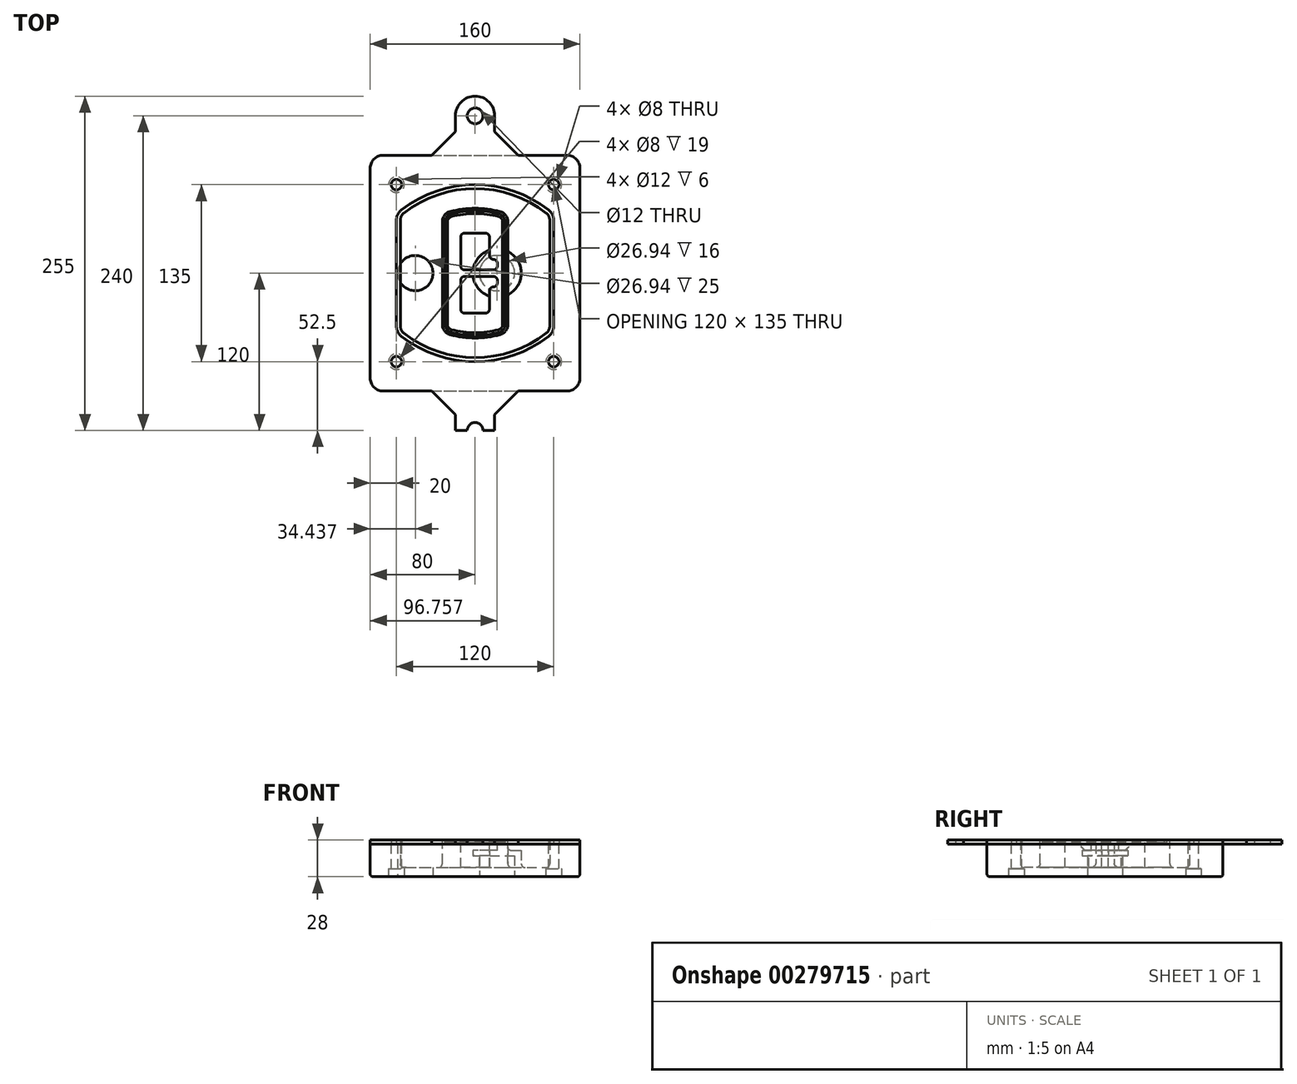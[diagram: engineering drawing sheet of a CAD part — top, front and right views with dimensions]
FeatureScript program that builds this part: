
annotation { "Feature Type Name" : "Feature", "Feature Type Description" : "" }
export const myFeature = defineFeature(function(context is Context, id is Id, definition is map)
    precondition{}
    {
        {
            var Q0;
            Q0=qCreatedBy(makeId("Top.planeOp"),FACE);
            var sketch = newSketch(context, id + "F0", { "sketchPlane" : qUnion([Q0])});
            skPoint(sketch, "E0.rect.middle", {"position": v(0, 0) * mm});
            skLineSegment(sketch, "E1.bottom", {"start": v(-70, -90) * mm, "end": v(70, -90) * mm});
            skLineSegment(sketch, "E1.top", {"start": v(-70, 90) * mm, "end": v(70, 90) * mm});
            skLineSegment(sketch, "E1.left", {"start": v(-80, -80) * mm, "end": v(-80, 80) * mm});
            skLineSegment(sketch, "E1.right", {"start": v(80, -80) * mm, "end": v(80, 80) * mm});
            skLineSegment(sketch, "E2", {"start": v(-80, 90) * mm, "end": v(80, -90) * mm, "construction": true});
            skLineSegment(sketch, "E3", {"start": v(80, 90) * mm, "end": v(-80, -90) * mm, "construction": true});
            skCircle(sketch, "E4", {"center": v(-60, 67.5) * mm, "radius": 4 * mm});
            skCircle(sketch, "E5", {"center": v(60, 67.5) * mm, "radius": 4 * mm});
            skCircle(sketch, "E6", {"center": v(60, -67.5) * mm, "radius": 4 * mm});
            skCircle(sketch, "E7", {"center": v(-60, -67.5) * mm, "radius": 4 * mm});
            skLineSegment(sketch, "E8", {"start": v(-60, 67.5) * mm, "end": v(60, 67.5) * mm, "construction": true});
            skLineSegment(sketch, "E9", {"start": v(60, 67.5) * mm, "end": v(60, -67.5) * mm, "construction": true});
            skLineSegment(sketch, "E10", {"start": v(60, -67.5) * mm, "end": v(-60, -67.5) * mm, "construction": true});
            skLineSegment(sketch, "E11", {"start": v(-60, -67.5) * mm, "end": v(-60, 67.5) * mm, "construction": true});
            skLineSegment(sketch, "E12", {"start": v(-60, 40.3) * mm, "end": v(-60, -40.3) * mm});
            skLineSegment(sketch, "E13", {"start": v(60, 40.3) * mm, "end": v(60, -40.3) * mm});
            skArc(sketch, "E14", {"start": v(56.15, 48.18) * mm, "mid": v(0, 67.5) * mm, "end": v(-56.15, 48.18) * mm});
            skArc(sketch, "E15", {"start": v(-56.15, -48.18) * mm, "mid": v(0, -67.5) * mm, "end": v(56.15, -48.18) * mm});
            skLineSegment(sketch, "E16", {"start": v(-60, 0) * mm, "end": v(60, 0) * mm, "construction": true});
            skPoint(sketch, "E17.visualSharp", {"position": v(-60, -45) * mm});
            skArc(sketch, "E17.filletArc", {"start": v(-60, -40.3) * mm, "mid": v(-58.99, -44.68) * mm, "end": v(-56.15, -48.18) * mm});
            skPoint(sketch, "E18.visualSharp", {"position": v(-60, 45) * mm});
            skArc(sketch, "E18.filletArc", {"start": v(-56.15, 48.18) * mm, "mid": v(-58.99, 44.68) * mm, "end": v(-60, 40.3) * mm});
            skPoint(sketch, "E19.visualSharp", {"position": v(60, 45) * mm});
            skArc(sketch, "E19.filletArc", {"start": v(60, 40.3) * mm, "mid": v(58.99, 44.68) * mm, "end": v(56.15, 48.18) * mm});
            skPoint(sketch, "E20.visualSharp", {"position": v(60, -45) * mm});
            skArc(sketch, "E20.filletArc", {"start": v(56.15, -48.18) * mm, "mid": v(58.99, -44.68) * mm, "end": v(60, -40.3) * mm});
            skPoint(sketch, "E21.visualSharp", {"position": v(-80, 90) * mm});
            skArc(sketch, "E21.filletArc", {"start": v(-70, 90) * mm, "mid": v(-77.07, 87.07) * mm, "end": v(-80, 80) * mm});
            skPoint(sketch, "E22.visualSharp", {"position": v(80, 90) * mm});
            skArc(sketch, "E22.filletArc", {"start": v(80, 80) * mm, "mid": v(77.07, 87.07) * mm, "end": v(70, 90) * mm});
            skPoint(sketch, "E23.visualSharp", {"position": v(80, -90) * mm});
            skArc(sketch, "E23.filletArc", {"start": v(70, -90) * mm, "mid": v(77.07, -87.07) * mm, "end": v(80, -80) * mm});
            skPoint(sketch, "E24.visualSharp", {"position": v(-80, -90) * mm});
            skArc(sketch, "E24.filletArc", {"start": v(-80, -80) * mm, "mid": v(-77.07, -87.07) * mm, "end": v(-70, -90) * mm});
            skArc(sketch, "E25.0", {"start": v(57, 40.3) * mm, "mid": v(56.3, 43.36) * mm, "end": v(54.3, 45.81) * mm});
            skLineSegment(sketch, "E25.1", {"start": v(57, 40.3) * mm, "end": v(57, -40.3) * mm});
            skArc(sketch, "E25.2", {"start": v(54.3, -45.81) * mm, "mid": v(56.3, -43.36) * mm, "end": v(57, -40.3) * mm});
            skArc(sketch, "E25.3", {"start": v(-54.3, -45.81) * mm, "mid": v(0, -64.5) * mm, "end": v(54.3, -45.81) * mm});
            skArc(sketch, "E25.4", {"start": v(-57, -40.3) * mm, "mid": v(-56.3, -43.36) * mm, "end": v(-54.3, -45.81) * mm});
            skArc(sketch, "E25.5", {"start": v(54.3, 45.81) * mm, "mid": v(0, 64.5) * mm, "end": v(-54.3, 45.81) * mm});
            skLineSegment(sketch, "E25.6", {"start": v(-57, 40.3) * mm, "end": v(-57, -40.3) * mm});
            skArc(sketch, "E25.7", {"start": v(-54.3, 45.81) * mm, "mid": v(-56.3, 43.36) * mm, "end": v(-57, 40.3) * mm});
            skArc(sketch, "E26.0", {"start": v(-58.62, 51.33) * mm, "mid": v(-62.58, 46.43) * mm, "end": v(-64, 40.3) * mm});
            skArc(sketch, "E26.1", {"start": v(58.62, 51.33) * mm, "mid": v(0, 71.5) * mm, "end": v(-58.62, 51.33) * mm});
            skArc(sketch, "E26.2", {"start": v(64, 40.3) * mm, "mid": v(62.58, 46.43) * mm, "end": v(58.62, 51.33) * mm});
            skLineSegment(sketch, "E26.3", {"start": v(64, 40.3) * mm, "end": v(64, -40.3) * mm});
            skArc(sketch, "E26.4", {"start": v(58.62, -51.33) * mm, "mid": v(62.58, -46.43) * mm, "end": v(64, -40.3) * mm});
            skLineSegment(sketch, "E26.5", {"start": v(-64, 40.3) * mm, "end": v(-64, -40.3) * mm});
            skArc(sketch, "E26.6", {"start": v(-58.62, -51.33) * mm, "mid": v(0, -71.5) * mm, "end": v(58.62, -51.33) * mm});
            skArc(sketch, "E26.7", {"start": v(-64, -40.3) * mm, "mid": v(-62.58, -46.43) * mm, "end": v(-58.62, -51.33) * mm});
            skSolve(sketch);
        }
        {
            var Q0;
            Q0=makeQuery(id+"F0.imprint","IMPRINT",FACE,{"disambiguationData":[TD([[makeQuery(id+"F0.imprint","IMPRINT",EDGE,{"derivedFrom":sQuery(id+"F0.wireOp",EDGE,"E1.bottom")}),1.0]])]});
            var Q1;
            Q1=makeQuery(id+"F0.imprint","IMPRINT",FACE,{"disambiguationData":[TD([[makeQuery(id+"F0.imprint","IMPRINT",EDGE,{"derivedFrom":sQuery(id+"F0.wireOp",EDGE,"E12")}),1.0]])]});
            var Q2;
            Q2=makeQuery(id+"F0.imprint","IMPRINT",FACE,{"disambiguationData":[TD([[makeQuery(id+"F0.imprint","IMPRINT",EDGE,{"derivedFrom":sQuery(id+"F0.wireOp",EDGE,"E25.0")}),1.0]])]});
            var Q3;
            Q3=makeQuery(id+"F0.imprint","IMPRINT",FACE,{"disambiguationData":[TD([[makeQuery(id+"F0.imprint","IMPRINT",EDGE,{"derivedFrom":sQuery(id+"F0.wireOp",EDGE,"E12")}),-1.0]])]});
            extrude(context, id + "F1", {"entities" : qUnion([Q0, Q1, Q2, Q3]), "oppositeDirection" : true, "depth" : 25 * mm});
        }
        {
            var Q0;
            Q0=makeQuery(id+"F0.imprint","IMPRINT",FACE,{"disambiguationData":[TD([[makeQuery(id+"F0.imprint","IMPRINT",EDGE,{"derivedFrom":sQuery(id+"F0.wireOp",EDGE,"E12")}),1.0]])]});
            extrude(context, id + "F2", {"entities" : qUnion([Q0]), "operationType" : NewBodyOperationType.ADD, "depth" : 3 * mm});
        }
        {
            var Q0;
            Q0=makeQuery(id+"F0.imprint","IMPRINT",FACE,{"disambiguationData":[TD([[makeQuery(id+"F0.imprint","IMPRINT",EDGE,{"derivedFrom":sQuery(id+"F0.wireOp",EDGE,"E25.0")}),1.0]])]});
            extrude(context, id + "F3", {"entities" : qUnion([Q0]), "operationType" : NewBodyOperationType.REMOVE, "oppositeDirection" : true, "depth" : 18 * mm});
        }
        {
            var Q0;
            Q0=makeQuery(id+"F2.opExtrude","CAP_FACE",FACE,{"disambiguationData":[OSD([sQuery(id+"F0.wireOp",EDGE,"E12"),sQuery(id+"F0.wireOp",EDGE,"E13"),sQuery(id+"F0.wireOp",EDGE,"E14"),sQuery(id+"F0.wireOp",EDGE,"E15"),sQuery(id+"F0.wireOp",EDGE,"E17.filletArc"),sQuery(id+"F0.wireOp",EDGE,"E18.filletArc"),sQuery(id+"F0.wireOp",EDGE,"E19.filletArc"),sQuery(id+"F0.wireOp",EDGE,"E20.filletArc"),sQuery(id+"F0.wireOp",EDGE,"E25.0"),sQuery(id+"F0.wireOp",EDGE,"E25.1"),sQuery(id+"F0.wireOp",EDGE,"E25.2"),sQuery(id+"F0.wireOp",EDGE,"E25.3"),sQuery(id+"F0.wireOp",EDGE,"E25.4"),sQuery(id+"F0.wireOp",EDGE,"E25.5"),sQuery(id+"F0.wireOp",EDGE,"E25.6"),sQuery(id+"F0.wireOp",EDGE,"E25.7")])],"isStart":false});
            var sketch = newSketch(context, id + "F4", { "sketchPlane" : qUnion([Q0])});
            skArc(sketch, "E27.0", {"start": v(-19.08, -46.97) * mm, "mid": v(0, -49.5) * mm, "end": v(19.08, -46.97) * mm});
            skArc(sketch, "E28.0", {"start": v(19.08, 46.97) * mm, "mid": v(0, 49.5) * mm, "end": v(-19.08, 46.97) * mm});
            skLineSegment(sketch, "E29", {"start": v(-25, 39.25) * mm, "end": v(-25, -39.25) * mm});
            skLineSegment(sketch, "E30", {"start": v(25, 39.25) * mm, "end": v(25, -39.25) * mm});
            skLineSegment(sketch, "E31", {"start": v(-25, 45.1) * mm, "end": v(25, 45.1) * mm, "construction": true});
            skLineSegment(sketch, "E32", {"start": v(-25, -45.1) * mm, "end": v(25, -45.1) * mm, "construction": true});
            skPoint(sketch, "E33.visualSharp", {"position": v(-25, 45.1) * mm});
            skArc(sketch, "E33.filletArc", {"start": v(-19.08, 46.97) * mm, "mid": v(-23.35, 44.11) * mm, "end": v(-25, 39.25) * mm});
            skPoint(sketch, "E34.visualSharp", {"position": v(25, 45.1) * mm});
            skArc(sketch, "E34.filletArc", {"start": v(25, 39.25) * mm, "mid": v(23.35, 44.11) * mm, "end": v(19.08, 46.97) * mm});
            skPoint(sketch, "E35.visualSharp", {"position": v(25, -45.1) * mm});
            skArc(sketch, "E35.filletArc", {"start": v(19.08, -46.97) * mm, "mid": v(23.35, -44.11) * mm, "end": v(25, -39.25) * mm});
            skPoint(sketch, "E36.visualSharp", {"position": v(-25, -45.1) * mm});
            skArc(sketch, "E36.filletArc", {"start": v(-25, -39.25) * mm, "mid": v(-23.35, -44.11) * mm, "end": v(-19.08, -46.97) * mm});
            skArc(sketch, "E37.0", {"start": v(54.3, 45.81) * mm, "mid": v(0, 64.5) * mm, "end": v(-54.3, 45.81) * mm});
            skArc(sketch, "E37.1", {"start": v(-54.3, 45.81) * mm, "mid": v(-56.3, 43.36) * mm, "end": v(-57, 40.3) * mm});
            skLineSegment(sketch, "E37.2", {"start": v(-57, 40.3) * mm, "end": v(-57, -40.3) * mm});
            skArc(sketch, "E37.3", {"start": v(-57, -40.3) * mm, "mid": v(-56.3, -43.36) * mm, "end": v(-54.3, -45.81) * mm});
            skArc(sketch, "E37.4", {"start": v(-54.3, -45.81) * mm, "mid": v(0, -64.5) * mm, "end": v(54.3, -45.81) * mm});
            skArc(sketch, "E37.5", {"start": v(54.3, -45.81) * mm, "mid": v(56.3, -43.36) * mm, "end": v(57, -40.3) * mm});
            skLineSegment(sketch, "E37.6", {"start": v(57, 40.3) * mm, "end": v(57, -40.3) * mm});
            skArc(sketch, "E37.7", {"start": v(57, 40.3) * mm, "mid": v(56.3, 43.36) * mm, "end": v(54.3, 45.81) * mm});
            skLineSegment(sketch, "E38.0", {"start": v(23, 39.25) * mm, "end": v(23, -39.25) * mm});
            skArc(sketch, "E38.1", {"start": v(18.56, -45.04) * mm, "mid": v(21.76, -42.9) * mm, "end": v(23, -39.25) * mm});
            skArc(sketch, "E38.2", {"start": v(-18.56, -45.04) * mm, "mid": v(0, -47.5) * mm, "end": v(18.56, -45.04) * mm});
            skArc(sketch, "E38.3", {"start": v(-23, -39.25) * mm, "mid": v(-21.76, -42.9) * mm, "end": v(-18.56, -45.04) * mm});
            skLineSegment(sketch, "E38.4", {"start": v(-23, 39.25) * mm, "end": v(-23, -39.25) * mm});
            skArc(sketch, "E38.5", {"start": v(23, 39.25) * mm, "mid": v(21.76, 42.9) * mm, "end": v(18.56, 45.04) * mm});
            skArc(sketch, "E38.6", {"start": v(-18.56, 45.04) * mm, "mid": v(-21.76, 42.9) * mm, "end": v(-23, 39.25) * mm});
            skArc(sketch, "E38.7", {"start": v(18.56, 45.04) * mm, "mid": v(0, 47.5) * mm, "end": v(-18.56, 45.04) * mm});
            skArc(sketch, "E39.0", {"start": v(21, 39.25) * mm, "mid": v(20.18, 41.68) * mm, "end": v(18.04, 43.1) * mm});
            skLineSegment(sketch, "E39.1", {"start": v(21, 39.25) * mm, "end": v(21, -39.25) * mm});
            skArc(sketch, "E39.2", {"start": v(18.04, -43.1) * mm, "mid": v(20.18, -41.68) * mm, "end": v(21, -39.25) * mm});
            skArc(sketch, "E39.3", {"start": v(-18.04, -43.1) * mm, "mid": v(0, -45.5) * mm, "end": v(18.04, -43.1) * mm});
            skArc(sketch, "E39.4", {"start": v(-21, -39.25) * mm, "mid": v(-20.18, -41.68) * mm, "end": v(-18.04, -43.1) * mm});
            skArc(sketch, "E39.5", {"start": v(18.04, 43.1) * mm, "mid": v(0, 45.5) * mm, "end": v(-18.04, 43.1) * mm});
            skLineSegment(sketch, "E39.6", {"start": v(-21, 39.25) * mm, "end": v(-21, -39.25) * mm});
            skArc(sketch, "E39.7", {"start": v(-18.04, 43.1) * mm, "mid": v(-20.18, 41.68) * mm, "end": v(-21, 39.25) * mm});
            skLineSegment(sketch, "E40", {"start": v(-25, 0) * mm, "end": v(25, 0) * mm, "construction": true});
            skLineSegment(sketch, "E41", {"start": v(-11, 5.5) * mm, "end": v(-11, 27.5) * mm});
            skLineSegment(sketch, "E42", {"start": v(-8, 30.5) * mm, "end": v(8, 30.5) * mm});
            skLineSegment(sketch, "E43", {"start": v(11, 27.5) * mm, "end": v(11, 13.5) * mm});
            skLineSegment(sketch, "E44", {"start": v(14, 10.5) * mm, "end": v(14, 10.5) * mm});
            skLineSegment(sketch, "E45", {"start": v(17, 7.5) * mm, "end": v(17, 5.5) * mm});
            skLineSegment(sketch, "E46", {"start": v(14, 2.5) * mm, "end": v(-8, 2.5) * mm});
            skPoint(sketch, "E47.visualSharp", {"position": v(-11, 30.5) * mm});
            skArc(sketch, "E47.filletArc", {"start": v(-8, 30.5) * mm, "mid": v(-10.12, 29.62) * mm, "end": v(-11, 27.5) * mm});
            skPoint(sketch, "E48.visualSharp", {"position": v(11, 30.5) * mm});
            skArc(sketch, "E48.filletArc", {"start": v(11, 27.5) * mm, "mid": v(10.12, 29.62) * mm, "end": v(8, 30.5) * mm});
            skPoint(sketch, "E49.visualSharp", {"position": v(11, 10.5) * mm});
            skArc(sketch, "E49.filletArc", {"start": v(11, 13.5) * mm, "mid": v(11.88, 11.38) * mm, "end": v(14, 10.5) * mm});
            skPoint(sketch, "E50.visualSharp", {"position": v(17, 10.5) * mm});
            skArc(sketch, "E50.filletArc", {"start": v(17, 7.5) * mm, "mid": v(16.12, 9.62) * mm, "end": v(14, 10.5) * mm});
            skPoint(sketch, "E51.visualSharp", {"position": v(17, 2.5) * mm});
            skArc(sketch, "E51.filletArc", {"start": v(14, 2.5) * mm, "mid": v(16.12, 3.38) * mm, "end": v(17, 5.5) * mm});
            skPoint(sketch, "E52.visualSharp", {"position": v(-11, 2.5) * mm});
            skArc(sketch, "E52.filletArc", {"start": v(-11, 5.5) * mm, "mid": v(-10.12, 3.38) * mm, "end": v(-8, 2.5) * mm});
            skLineSegment(sketch, "E53.0.MirrorCS", {"start": v(14, -2.5) * mm, "end": v(-8, -2.5) * mm});
            skArc(sketch, "E54.0.MirrorCS", {"start": v(-11, -5.5) * mm, "mid": v(-10.12, -3.38) * mm, "end": v(-8, -2.5) * mm});
            skLineSegment(sketch, "E55.0.MirrorCS", {"start": v(-11, -5.5) * mm, "end": v(-11, -27.5) * mm});
            skArc(sketch, "E56.0.MirrorCS", {"start": v(-8, -30.5) * mm, "mid": v(-10.12, -29.62) * mm, "end": v(-11, -27.5) * mm});
            skLineSegment(sketch, "E57.0.MirrorCS", {"start": v(-8, -30.5) * mm, "end": v(8, -30.5) * mm});
            skArc(sketch, "E58.0.MirrorCS", {"start": v(11, -27.5) * mm, "mid": v(10.12, -29.62) * mm, "end": v(8, -30.5) * mm});
            skLineSegment(sketch, "E59.0.MirrorCS", {"start": v(11, -27.5) * mm, "end": v(11, -13.5) * mm});
            skArc(sketch, "E60.0.MirrorCS", {"start": v(11, -13.5) * mm, "mid": v(11.88, -11.38) * mm, "end": v(14, -10.5) * mm});
            skArc(sketch, "E61.0.MirrorCS", {"start": v(17, -7.5) * mm, "mid": v(16.12, -9.62) * mm, "end": v(14, -10.5) * mm});
            skLineSegment(sketch, "E62.0.MirrorCS", {"start": v(17, -7.5) * mm, "end": v(17, -5.5) * mm});
            skArc(sketch, "E63.0.MirrorCS", {"start": v(14, -2.5) * mm, "mid": v(16.12, -3.38) * mm, "end": v(17, -5.5) * mm});
            skSolve(sketch);
        }
        {
            var Q0;
            Q0=makeQuery(id+"F4.imprint","IMPRINT",FACE,{"disambiguationData":[TD([[makeQuery(id+"F4.imprint","IMPRINT",EDGE,{"derivedFrom":sQuery(id+"F4.wireOp",EDGE,"E27.0")}),1.0]])]});
            var Q1;
            Q1=makeQuery(id+"F4.imprint","IMPRINT",FACE,{"disambiguationData":[TD([[makeQuery(id+"F4.imprint","IMPRINT",EDGE,{"derivedFrom":sQuery(id+"F4.wireOp",EDGE,"E38.0")}),-1.0]])]});
            var Q2;
            Q2=makeQuery(id+"F4.imprint","IMPRINT",FACE,{"disambiguationData":[TD([[makeQuery(id+"F4.imprint","IMPRINT",EDGE,{"derivedFrom":sQuery(id+"F4.wireOp",EDGE,"E39.0")}),1.0]])]});
            extrude(context, id + "F5", {"entities" : qUnion([Q0, Q1, Q2]), "operationType" : NewBodyOperationType.ADD, "endBound" : BoundingType.UP_TO_NEXT, "oppositeDirection" : true, "depth" : 25 * mm});
        }
        {
            var Q0;
            Q0=makeQuery(id+"F4.imprint","IMPRINT",FACE,{"disambiguationData":[TD([[makeQuery(id+"F4.imprint","IMPRINT",EDGE,{"derivedFrom":sQuery(id+"F4.wireOp",EDGE,"E38.0")}),-1.0]])]});
            extrude(context, id + "F6", {"entities" : qUnion([Q0]), "operationType" : NewBodyOperationType.REMOVE, "oppositeDirection" : true, "depth" : 2 * mm});
        }
        {
            var Q0;
            Q0=makeQuery(id+"F1.opExtrude","CAP_FACE",FACE,{"disambiguationData":[OSD([sQuery(id+"F0.wireOp",EDGE,"E1.bottom"),sQuery(id+"F0.wireOp",EDGE,"E1.top"),sQuery(id+"F0.wireOp",EDGE,"E1.left"),sQuery(id+"F0.wireOp",EDGE,"E1.right"),sQuery(id+"F0.wireOp",EDGE,"E4"),sQuery(id+"F0.wireOp",EDGE,"E5"),sQuery(id+"F0.wireOp",EDGE,"E6"),sQuery(id+"F0.wireOp",EDGE,"E7"),sQuery(id+"F0.wireOp",EDGE,"E21.filletArc"),sQuery(id+"F0.wireOp",EDGE,"E22.filletArc"),sQuery(id+"F0.wireOp",EDGE,"E23.filletArc"),sQuery(id+"F0.wireOp",EDGE,"E24.filletArc")])],"isStart":false});
            var sketch = newSketch(context, id + "F7", { "sketchPlane" : qUnion([Q0])});
            skCircle(sketch, "E64", {"center": v(16.76, 0) * mm, "radius": 13.47 * mm});
            skCircle(sketch, "E65", {"center": v(-45.56, 0) * mm, "radius": 13.47 * mm});
            skLineSegment(sketch, "E66", {"start": v(80, 0) * mm, "end": v(-80, 0) * mm});
            skCircle(sketch, "E67", {"center": v(16.76, 0) * mm, "radius": 18.47 * mm});
            skCircle(sketch, "E68", {"center": v(60, -67.5) * mm, "radius": 6 * mm});
            skCircle(sketch, "E69", {"center": v(-60, -67.5) * mm, "radius": 6 * mm});
            skCircle(sketch, "E70", {"center": v(-60, 67.5) * mm, "radius": 6 * mm});
            skCircle(sketch, "E71", {"center": v(60, 67.5) * mm, "radius": 6 * mm});
            skSolve(sketch);
        }
        {
            var Q0;
            {var subQ1=sQuery(id+"F7.wireOp",EDGE,"E66");var subQ4=sQuery(id+"F7.wireOp",EDGE,"E64");var subQ6=makeQuery(id+"F7.imprint","INTERSECT",VERTEX,{"disambiguationData":[OD(0.0)],"derivedFrom":[subQ4,subQ1]});Q0=makeQuery(id+"F7.imprint","IMPRINT",FACE,{"disambiguationData":[TD([[makeQuery(id+"F7.imprint","IMPRINT",EDGE,{"disambiguationData":[TD([[subQ6,-1.0]])],"derivedFrom":subQ4}),-1.0]])]});}
            var Q1;
            {var subQ0=sQuery(id+"F7.wireOp",EDGE,"E66");var subQ1=sQuery(id+"F7.wireOp",EDGE,"E64");var subQ3=makeQuery(id+"F7.imprint","INTERSECT",VERTEX,{"disambiguationData":[OD(0.0)],"derivedFrom":[subQ1,subQ0]});Q1=makeQuery(id+"F7.imprint","IMPRINT",FACE,{"disambiguationData":[TD([[makeQuery(id+"F7.imprint","IMPRINT",EDGE,{"disambiguationData":[TD([[subQ3,-1.0]])],"derivedFrom":subQ1}),1.0]])]});}
            var Q2;
            {var subQ0=sQuery(id+"F7.wireOp",EDGE,"E66");var subQ1=sQuery(id+"F7.wireOp",EDGE,"E64");var subQ3=makeQuery(id+"F7.imprint","INTERSECT",VERTEX,{"disambiguationData":[OD(0.0)],"derivedFrom":[subQ1,subQ0]});Q2=makeQuery(id+"F7.imprint","IMPRINT",FACE,{"disambiguationData":[TD([[makeQuery(id+"F7.imprint","IMPRINT",EDGE,{"disambiguationData":[TD([[subQ3,1.0]])],"derivedFrom":subQ1}),1.0]])]});}
            var Q3;
            {var subQ1=sQuery(id+"F7.wireOp",EDGE,"E66");var subQ4=sQuery(id+"F7.wireOp",EDGE,"E64");var subQ6=makeQuery(id+"F7.imprint","INTERSECT",VERTEX,{"disambiguationData":[OD(0.0)],"derivedFrom":[subQ4,subQ1]});Q3=makeQuery(id+"F7.imprint","IMPRINT",FACE,{"disambiguationData":[TD([[makeQuery(id+"F7.imprint","IMPRINT",EDGE,{"disambiguationData":[TD([[subQ6,1.0]])],"derivedFrom":subQ4}),-1.0]])]});}
            extrude(context, id + "F8", {"entities" : qUnion([Q0, Q1, Q2, Q3]), "operationType" : NewBodyOperationType.ADD, "oppositeDirection" : true, "depth" : 20 * mm});
        }
        {
            var Q0;
            {var subQ0=sQuery(id+"F7.wireOp",EDGE,"E66");var subQ1=sQuery(id+"F7.wireOp",EDGE,"E64");var subQ3=makeQuery(id+"F7.imprint","INTERSECT",VERTEX,{"disambiguationData":[OD(0.0)],"derivedFrom":[subQ1,subQ0]});Q0=makeQuery(id+"F7.imprint","IMPRINT",FACE,{"disambiguationData":[TD([[makeQuery(id+"F7.imprint","IMPRINT",EDGE,{"disambiguationData":[TD([[subQ3,-1.0]])],"derivedFrom":subQ1}),1.0]])]});}
            var Q1;
            {var subQ0=sQuery(id+"F7.wireOp",EDGE,"E66");var subQ1=sQuery(id+"F7.wireOp",EDGE,"E64");var subQ3=makeQuery(id+"F7.imprint","INTERSECT",VERTEX,{"disambiguationData":[OD(0.0)],"derivedFrom":[subQ1,subQ0]});Q1=makeQuery(id+"F7.imprint","IMPRINT",FACE,{"disambiguationData":[TD([[makeQuery(id+"F7.imprint","IMPRINT",EDGE,{"disambiguationData":[TD([[subQ3,1.0]])],"derivedFrom":subQ1}),1.0]])]});}
            extrude(context, id + "F9", {"entities" : qUnion([Q0, Q1]), "operationType" : NewBodyOperationType.REMOVE, "oppositeDirection" : true, "depth" : 16 * mm});
        }
        {
            var Q0;
            {var subQ0=sQuery(id+"F7.wireOp",EDGE,"E66");var subQ1=sQuery(id+"F7.wireOp",EDGE,"E65");var subQ3=makeQuery(id+"F7.imprint","INTERSECT",VERTEX,{"disambiguationData":[OD(0.0)],"derivedFrom":[subQ1,subQ0]});Q0=makeQuery(id+"F7.imprint","IMPRINT",FACE,{"disambiguationData":[TD([[makeQuery(id+"F7.imprint","IMPRINT",EDGE,{"disambiguationData":[TD([[subQ3,-1.0]])],"derivedFrom":subQ1}),1.0]])]});}
            var Q1;
            {var subQ0=sQuery(id+"F7.wireOp",EDGE,"E66");var subQ1=sQuery(id+"F7.wireOp",EDGE,"E65");var subQ3=makeQuery(id+"F7.imprint","INTERSECT",VERTEX,{"disambiguationData":[OD(0.0)],"derivedFrom":[subQ1,subQ0]});Q1=makeQuery(id+"F7.imprint","IMPRINT",FACE,{"disambiguationData":[TD([[makeQuery(id+"F7.imprint","IMPRINT",EDGE,{"disambiguationData":[TD([[subQ3,1.0]])],"derivedFrom":subQ1}),1.0]])]});}
            extrude(context, id + "F10", {"entities" : qUnion([Q0, Q1]), "operationType" : NewBodyOperationType.REMOVE, "oppositeDirection" : true, "depth" : 25 * mm});
        }
        {
            var Q0;
            Q0=makeQuery(id+"F7.imprint","IMPRINT",FACE,{"disambiguationData":[TD([[makeQuery(id+"F7.imprint","IMPRINT",EDGE,{"derivedFrom":sQuery(id+"F7.wireOp",EDGE,"E68")}),1.0]])]});
            var Q1;
            Q1=makeQuery(id+"F7.imprint","IMPRINT",FACE,{"disambiguationData":[TD([[makeQuery(id+"F7.imprint","IMPRINT",EDGE,{"derivedFrom":makeQuery(id+"F1.opExtrude","CAP_EDGE",EDGE,{"disambiguationData":[OSD([sQuery(id+"F0.wireOp",EDGE,"E5")])],"isStart":false})}),-1.0]])]});
            var Q2;
            Q2=makeQuery(id+"F7.imprint","IMPRINT",FACE,{"disambiguationData":[TD([[makeQuery(id+"F7.imprint","IMPRINT",EDGE,{"derivedFrom":sQuery(id+"F7.wireOp",EDGE,"E69")}),1.0]])]});
            var Q3;
            Q3=makeQuery(id+"F7.imprint","IMPRINT",FACE,{"disambiguationData":[TD([[makeQuery(id+"F7.imprint","IMPRINT",EDGE,{"derivedFrom":makeQuery(id+"F1.opExtrude","CAP_EDGE",EDGE,{"disambiguationData":[OSD([sQuery(id+"F0.wireOp",EDGE,"E4")])],"isStart":false})}),-1.0]])]});
            var Q4;
            Q4=makeQuery(id+"F7.imprint","IMPRINT",FACE,{"disambiguationData":[TD([[makeQuery(id+"F7.imprint","IMPRINT",EDGE,{"derivedFrom":sQuery(id+"F7.wireOp",EDGE,"E70")}),1.0]])]});
            var Q5;
            Q5=makeQuery(id+"F7.imprint","IMPRINT",FACE,{"disambiguationData":[TD([[makeQuery(id+"F7.imprint","IMPRINT",EDGE,{"derivedFrom":makeQuery(id+"F1.opExtrude","CAP_EDGE",EDGE,{"disambiguationData":[OSD([sQuery(id+"F0.wireOp",EDGE,"E7")])],"isStart":false})}),-1.0]])]});
            var Q6;
            Q6=makeQuery(id+"F7.imprint","IMPRINT",FACE,{"disambiguationData":[TD([[makeQuery(id+"F7.imprint","IMPRINT",EDGE,{"derivedFrom":sQuery(id+"F7.wireOp",EDGE,"E71")}),1.0]])]});
            var Q7;
            Q7=makeQuery(id+"F7.imprint","IMPRINT",FACE,{"disambiguationData":[TD([[makeQuery(id+"F7.imprint","IMPRINT",EDGE,{"derivedFrom":makeQuery(id+"F1.opExtrude","CAP_EDGE",EDGE,{"disambiguationData":[OSD([sQuery(id+"F0.wireOp",EDGE,"E6")])],"isStart":false})}),-1.0]])]});
            extrude(context, id + "F11", {"entities" : qUnion([Q0, Q1, Q2, Q3, Q4, Q5, Q6, Q7]), "operationType" : NewBodyOperationType.REMOVE, "oppositeDirection" : true, "depth" : 6 * mm});
        }
        {
            var Q0;
            Q0=makeQuery(id+"F9.boolean.opBoolean","COPY",FACE,{"derivedFrom":makeQuery(id+"F9.opExtrude","CAP_FACE",FACE,{"disambiguationData":[OSD([sQuery(id+"F7.wireOp",EDGE,"E64")])],"isStart":false})});
            var sketch = newSketch(context, id + "F12", { "sketchPlane" : qUnion([Q0])});
            skArc(sketch, "E72.0", {"start": v(11, 17.55) * mm, "mid": v(2.57, 11.82) * mm, "end": v(-1.54, 2.5) * mm});
            skArc(sketch, "E72.1", {"start": v(-1.54, -2.5) * mm, "mid": v(2.57, -11.82) * mm, "end": v(11, -17.55) * mm});
            skLineSegment(sketch, "E73", {"start": v(-1.54, -2.5) * mm, "end": v(14, -2.5) * mm});
            skLineSegment(sketch, "E74.0", {"start": v(14, 2.5) * mm, "end": v(-1.54, 2.5) * mm});
            skArc(sketch, "E74.1", {"start": v(14, 2.5) * mm, "mid": v(16.12, 3.38) * mm, "end": v(17, 5.5) * mm});
            skLineSegment(sketch, "E74.2", {"start": v(17, 7.5) * mm, "end": v(17, 5.5) * mm});
            skArc(sketch, "E74.3", {"start": v(17, 7.5) * mm, "mid": v(16.12, 9.62) * mm, "end": v(14, 10.5) * mm});
            skArc(sketch, "E74.4", {"start": v(11, 13.5) * mm, "mid": v(11.88, 11.38) * mm, "end": v(14, 10.5) * mm});
            skLineSegment(sketch, "E74.5", {"start": v(11, 17.55) * mm, "end": v(11, 13.5) * mm});
            skLineSegment(sketch, "E74.7", {"start": v(14, -2.5) * mm, "end": v(-1.54, -2.5) * mm});
            skArc(sketch, "E74.8", {"start": v(14, -2.5) * mm, "mid": v(16.12, -3.38) * mm, "end": v(17, -5.5) * mm});
            skLineSegment(sketch, "E74.9", {"start": v(17, -7.5) * mm, "end": v(17, -5.5) * mm});
            skArc(sketch, "E74.10", {"start": v(17, -7.5) * mm, "mid": v(16.12, -9.62) * mm, "end": v(14, -10.5) * mm});
            skArc(sketch, "E74.11", {"start": v(11, -13.5) * mm, "mid": v(11.88, -11.38) * mm, "end": v(14, -10.5) * mm});
            skLineSegment(sketch, "E74.12", {"start": v(11, -17.55) * mm, "end": v(11, -13.5) * mm});
            skPoint(sketch, "E75.orphan", {"position": v(11, -27.5) * mm});
            skPoint(sketch, "E76.orphan", {"position": v(-8, -2.5) * mm});
            skPoint(sketch, "E77.orphan", {"position": v(-8, 2.5) * mm});
            skPoint(sketch, "E78.orphan", {"position": v(11, 27.5) * mm});
            skSolve(sketch);
        }
        {
            var Q0;
            {var subQ7=sQuery(id+"F12.wireOp",EDGE,"E72.0");var subQ14=sQuery(id+"F12.wireOp",EDGE,"E72.1");var subQ16=sQuery(id+"F12.wireOp",EDGE,"E74.1");var subQ18=sQuery(id+"F12.wireOp",EDGE,"E74.8");Q0=qUnion([makeQuery(id+"F12.imprint","IMPRINT",FACE,{"disambiguationData":[TD([[makeQuery(id+"F12.imprint","IMPRINT",EDGE,{"derivedFrom":subQ7}),1.0]])]}),makeQuery(id+"F12.imprint","IMPRINT",FACE,{"disambiguationData":[TD([[makeQuery(id+"F12.imprint","IMPRINT",EDGE,{"derivedFrom":subQ14}),1.0]])]}),makeQuery(id+"F12.imprint","IMPRINT",FACE,{"disambiguationData":[TD([[makeQuery(id+"F12.imprint","IMPRINT",EDGE,{"derivedFrom":subQ16}),1.0]])]}),makeQuery(id+"F12.imprint","IMPRINT",FACE,{"disambiguationData":[TD([[makeQuery(id+"F12.imprint","IMPRINT",EDGE,{"derivedFrom":subQ18}),-1.0]])]})]);}
            var Q1;
            Q1=makeQuery(id+"F5.boolean.opBoolean","SPLIT",FACE,{"disambiguationData":[TD([makeQuery(id+"F5.opExtrude","SWEPT_FACE",FACE,{"disambiguationData":[OSD([sQuery(id+"F4.wireOp",EDGE,"E41")])]})])],"derivedFrom":makeQuery(id+"F3.boolean.opBoolean","COPY",FACE,{"derivedFrom":makeQuery(id+"F3.opExtrude","CAP_FACE",FACE,{"disambiguationData":[OSD([sQuery(id+"F0.wireOp",EDGE,"E25.0"),sQuery(id+"F0.wireOp",EDGE,"E25.1"),sQuery(id+"F0.wireOp",EDGE,"E25.2"),sQuery(id+"F0.wireOp",EDGE,"E25.3"),sQuery(id+"F0.wireOp",EDGE,"E25.4"),sQuery(id+"F0.wireOp",EDGE,"E25.5"),sQuery(id+"F0.wireOp",EDGE,"E25.6"),sQuery(id+"F0.wireOp",EDGE,"E25.7")])],"isStart":false})})});
            extrude(context, id + "F13", {"entities" : qUnion([Q0]), "operationType" : NewBodyOperationType.REMOVE, "endBound" : BoundingType.UP_TO_SURFACE, "endBoundEntityFace" : qUnion([Q1]), "depth" : 25 * mm});
        }
        {
            var Q0;
            Q0=makeQuery(id+"F3.boolean.opBoolean","COPY",EDGE,{"derivedFrom":makeQuery(id+"F3.opExtrude","CAP_EDGE",EDGE,{"disambiguationData":[OSD([sQuery(id+"F0.wireOp",EDGE,"E25.6")])],"isStart":false})});
            var Q1;
            Q1=makeQuery(id+"F8.boolean.opBoolean","INTERSECT",EDGE,{"derivedFrom":[makeQuery(id+"F5.opExtrude","SWEPT_FACE",FACE,{"disambiguationData":[OSD([sQuery(id+"F4.wireOp",EDGE,"E30")])]}),makeQuery(id+"F8.opExtrude","CAP_FACE",FACE,{"disambiguationData":[OSD([sQuery(id+"F7.wireOp",EDGE,"E67")])],"isStart":false})]});
            var Q2;
            Q2=makeQuery(id+"F8.boolean.opBoolean","INTERSECT",EDGE,{"disambiguationData":[OD(1.0)],"derivedFrom":[makeQuery(id+"F5.opExtrude","SWEPT_FACE",FACE,{"disambiguationData":[OSD([sQuery(id+"F4.wireOp",EDGE,"E30")])]}),makeQuery(id+"F8.opExtrude","SWEPT_FACE",FACE,{"disambiguationData":[OSD([sQuery(id+"F7.wireOp",EDGE,"E67")])]})]});
            var Q3;
            {var subQ0=sQuery(id+"F4.wireOp",EDGE,"E30");Q3=makeQuery(id+"F8.boolean.opBoolean","SPLIT",EDGE,{"disambiguationData":[TD([makeQuery(id+"F5.opExtrude","SWEPT_FACE",FACE,{"disambiguationData":[OSD([sQuery(id+"F4.wireOp",EDGE,"E35.filletArc")])]})])],"derivedFrom":makeQuery(id+"F5.opExtrude","CAP_EDGE",EDGE,{"disambiguationData":[OSD([subQ0])],"isStart":false})});}
            var Q4;
            {var subQ0=sQuery(id+"F0.wireOp",EDGE,"E25.7");var subQ1=sQuery(id+"F0.wireOp",EDGE,"E25.1");var subQ2=sQuery(id+"F0.wireOp",EDGE,"E25.6");var subQ3=sQuery(id+"F0.wireOp",EDGE,"E25.5");var subQ4=sQuery(id+"F0.wireOp",EDGE,"E25.4");var subQ5=sQuery(id+"F0.wireOp",EDGE,"E25.0");var subQ6=sQuery(id+"F0.wireOp",EDGE,"E25.2");var subQ7=sQuery(id+"F0.wireOp",EDGE,"E25.3");Q4=makeQuery(id+"F8.boolean.opBoolean","INTERSECT",EDGE,{"derivedFrom":[makeQuery(id+"F5.boolean.opBoolean","SPLIT",FACE,{"disambiguationData":[TD([makeQuery(id+"F2.opExtrude","SWEPT_FACE",FACE,{"disambiguationData":[OSD([subQ5])]})])],"derivedFrom":makeQuery(id+"F3.boolean.opBoolean","COPY",FACE,{"derivedFrom":makeQuery(id+"F3.opExtrude","CAP_FACE",FACE,{"disambiguationData":[OSD([subQ5,subQ1,subQ6,subQ7,subQ4,subQ3,subQ2,subQ0])],"isStart":false})})}),makeQuery(id+"F8.opExtrude","SWEPT_FACE",FACE,{"disambiguationData":[OSD([sQuery(id+"F7.wireOp",EDGE,"E67")])]})]});}
            var Q5;
            Q5=makeQuery(id+"F8.boolean.opBoolean","INTERSECT",EDGE,{"disambiguationData":[OD(0.0)],"derivedFrom":[makeQuery(id+"F5.opExtrude","SWEPT_FACE",FACE,{"disambiguationData":[OSD([sQuery(id+"F4.wireOp",EDGE,"E30")])]}),makeQuery(id+"F8.opExtrude","SWEPT_FACE",FACE,{"disambiguationData":[OSD([sQuery(id+"F7.wireOp",EDGE,"E67")])]})]});
            fillet(context, id + "F14", {"entities" : qUnion([Q0, Q1, Q2, Q3, Q4, Q5]), "radius" : 3 * mm, "tangentPropagation" : true, "allowEdgeOverflow" : false});
        }
        {
            var Q0;
            Q0=makeQuery(id+"F1.opExtrude","CAP_EDGE",EDGE,{"disambiguationData":[OSD([sQuery(id+"F0.wireOp",EDGE,"E1.bottom")])],"isStart":false});
            fillet(context, id + "F15", {"entities" : qUnion([Q0]), "radius" : 2 * mm, "tangentPropagation" : true, "allowEdgeOverflow" : false});
        }
        {
            var Q0;
            {var subQ0=sQuery(id+"F0.wireOp",EDGE,"E22.filletArc");var subQ1=sQuery(id+"F0.wireOp",EDGE,"E7");var subQ2=sQuery(id+"F0.wireOp",EDGE,"E6");var subQ3=sQuery(id+"F0.wireOp",EDGE,"E5");var subQ4=sQuery(id+"F0.wireOp",EDGE,"E4");var subQ5=sQuery(id+"F0.wireOp",EDGE,"E1.bottom");var subQ6=sQuery(id+"F0.wireOp",EDGE,"E21.filletArc");var subQ7=sQuery(id+"F0.wireOp",EDGE,"E1.top");var subQ8=sQuery(id+"F0.wireOp",EDGE,"E1.left");var subQ9=sQuery(id+"F0.wireOp",EDGE,"E1.right");var subQ10=sQuery(id+"F0.wireOp",EDGE,"E23.filletArc");var subQ11=sQuery(id+"F0.wireOp",EDGE,"E24.filletArc");Q0=makeQuery(id+"F2.boolean.opBoolean","SPLIT",FACE,{"disambiguationData":[TD([makeQuery(id+"F1.opExtrude","SWEPT_FACE",FACE,{"disambiguationData":[OSD([subQ5])]})])],"derivedFrom":makeQuery(id+"F1.opExtrude","CAP_FACE",FACE,{"disambiguationData":[OSD([subQ5,subQ7,subQ8,subQ9,subQ4,subQ3,subQ2,subQ1,subQ6,subQ0,subQ10,subQ11])],"isStart":true})});}
            var sketch = newSketch(context, id + "F16", { "sketchPlane" : qUnion([Q0])});
            skLineSegment(sketch, "E79.0.0", {"start": v(70, 90) * mm, "end": v(-70, 90) * mm});
            skArc(sketch, "E79.0.1", {"start": v(-70, 90) * mm, "mid": v(-77.07, 87.07) * mm, "end": v(-80, 80) * mm});
            skLineSegment(sketch, "E79.0.2", {"start": v(-80, 80) * mm, "end": v(-80, -80) * mm});
            skArc(sketch, "E79.0.3", {"start": v(-80, -80) * mm, "mid": v(-77.07, -87.07) * mm, "end": v(-70, -90) * mm});
            skLineSegment(sketch, "E79.0.4", {"start": v(-70, -90) * mm, "end": v(70, -90) * mm});
            skArc(sketch, "E79.0.5", {"start": v(70, -90) * mm, "mid": v(77.07, -87.07) * mm, "end": v(80, -80) * mm});
            skLineSegment(sketch, "E79.0.6", {"start": v(80, -80) * mm, "end": v(80, 80) * mm});
            skArc(sketch, "E79.0.7", {"start": v(80, 80) * mm, "mid": v(77.07, 87.07) * mm, "end": v(70, 90) * mm});
            skCircle(sketch, "E80.0", {"center": v(-60, 67.5) * mm, "radius": 4 * mm});
            skCircle(sketch, "E81.0", {"center": v(-60, -67.5) * mm, "radius": 4 * mm});
            skCircle(sketch, "E82.0", {"center": v(60, -67.5) * mm, "radius": 4 * mm});
            skCircle(sketch, "E83.0", {"center": v(60, 67.5) * mm, "radius": 4 * mm});
            skLineSegment(sketch, "E84.0.0", {"start": v(60, -40.3) * mm, "end": v(60, 40.3) * mm});
            skArc(sketch, "E84.0.1", {"start": v(60, 40.3) * mm, "mid": v(58.99, 44.68) * mm, "end": v(56.15, 48.18) * mm});
            skArc(sketch, "E84.0.2", {"start": v(56.15, 48.18) * mm, "mid": v(0, 67.5) * mm, "end": v(-56.15, 48.18) * mm});
            skArc(sketch, "E84.0.3", {"start": v(-56.15, 48.18) * mm, "mid": v(-58.99, 44.68) * mm, "end": v(-60, 40.3) * mm});
            skLineSegment(sketch, "E84.0.4", {"start": v(-60, 40.3) * mm, "end": v(-60, -40.3) * mm});
            skArc(sketch, "E84.0.5", {"start": v(-60, -40.3) * mm, "mid": v(-58.99, -44.68) * mm, "end": v(-56.15, -48.18) * mm});
            skArc(sketch, "E84.0.6", {"start": v(-56.15, -48.18) * mm, "mid": v(0, -67.5) * mm, "end": v(56.15, -48.18) * mm});
            skArc(sketch, "E84.0.7", {"start": v(56.15, -48.18) * mm, "mid": v(58.99, -44.68) * mm, "end": v(60, -40.3) * mm});
            skLineSegment(sketch, "E85", {"start": v(0, 90) * mm, "end": v(0, 120) * mm, "construction": true});
            skPoint(sketch, "E85.endSnap0", {"position": v(0, 90) * mm});
            skLineSegment(sketch, "E86", {"start": v(-33, 90) * mm, "end": v(-15, 108) * mm});
            skLineSegment(sketch, "E87", {"start": v(-15, 108) * mm, "end": v(-15, 120) * mm});
            skLineSegment(sketch, "E88", {"start": v(-15, 120) * mm, "end": v(15, 120) * mm});
            skLineSegment(sketch, "E89", {"start": v(15, 120) * mm, "end": v(15, 108) * mm});
            skLineSegment(sketch, "E90", {"start": v(15, 108) * mm, "end": v(33, 90) * mm});
            skArc(sketch, "E91", {"start": v(15, 120) * mm, "mid": v(0, 135) * mm, "end": v(-15, 120) * mm});
            skCircle(sketch, "E92", {"center": v(0, 120) * mm, "radius": 6 * mm});
            skLineSegment(sketch, "E93", {"start": v(-80, 0) * mm, "end": v(80, 0) * mm, "construction": true});
            skPoint(sketch, "E94.MirrorP", {"position": v(0, -90) * mm});
            skLineSegment(sketch, "E95.MirrorCS", {"start": v(0, -90) * mm, "end": v(0, -120) * mm, "construction": true});
            skLineSegment(sketch, "E96.MirrorCS", {"start": v(15, -108) * mm, "end": v(33, -90) * mm});
            skLineSegment(sketch, "E97.MirrorCS", {"start": v(-33, -90) * mm, "end": v(-15, -108) * mm});
            skLineSegment(sketch, "E98.MirrorCS", {"start": v(-15, -120) * mm, "end": v(15, -120) * mm});
            skLineSegment(sketch, "E99.MirrorCS", {"start": v(-15, -108) * mm, "end": v(-15, -120) * mm});
            skLineSegment(sketch, "E100.MirrorCS", {"start": v(15, -120) * mm, "end": v(15, -108) * mm});
            skArc(sketch, "E101.MirrorCS", {"start": v(15, -120) * mm, "mid": v(0, -135) * mm, "end": v(-15, -120) * mm});
            skCircle(sketch, "E102.MirrorC", {"center": v(0, -120) * mm, "radius": 6 * mm});
            skSolve(sketch);
        }
        {
            var Q0;
            {var subQ7=sQuery(id+"F16.wireOp",EDGE,"E86");Q0=makeQuery(id+"F16.imprint","IMPRINT",FACE,{"disambiguationData":[TD([[makeQuery(id+"F16.imprint","IMPRINT",EDGE,{"derivedFrom":subQ7}),-1.0]])]});}
            var Q1;
            {var subQ0=sQuery(id+"F16.wireOp",EDGE,"E91");Q1=makeQuery(id+"F16.imprint","IMPRINT",FACE,{"disambiguationData":[TD([[makeQuery(id+"F16.imprint","IMPRINT",EDGE,{"derivedFrom":subQ0}),1.0]])]});}
            var Q2;
            {var subQ0=sQuery(id+"F16.wireOp",EDGE,"E101.MirrorCS");Q2=makeQuery(id+"F16.imprint","IMPRINT",FACE,{"disambiguationData":[TD([[makeQuery(id+"F16.imprint","IMPRINT",EDGE,{"derivedFrom":subQ0}),-1.0]])]});}
            var Q3;
            {var subQ6=sQuery(id+"F16.wireOp",EDGE,"E96.MirrorCS");Q3=makeQuery(id+"F16.imprint","IMPRINT",FACE,{"disambiguationData":[TD([[makeQuery(id+"F16.imprint","IMPRINT",EDGE,{"derivedFrom":subQ6}),1.0]])]});}
            var Q4;
            {var subQ1=sQuery(id+"F16.wireOp",EDGE,"E79.0.1");Q4=makeQuery(id+"F16.imprint","IMPRINT",FACE,{"disambiguationData":[TD([[makeQuery(id+"F16.imprint","IMPRINT",EDGE,{"derivedFrom":subQ1}),1.0]])]});}
            var Q5;
            Q5=makeQuery(id+"F2.opExtrude","CAP_FACE",FACE,{"disambiguationData":[OSD([sQuery(id+"F0.wireOp",EDGE,"E12"),sQuery(id+"F0.wireOp",EDGE,"E13"),sQuery(id+"F0.wireOp",EDGE,"E14"),sQuery(id+"F0.wireOp",EDGE,"E15"),sQuery(id+"F0.wireOp",EDGE,"E17.filletArc"),sQuery(id+"F0.wireOp",EDGE,"E18.filletArc"),sQuery(id+"F0.wireOp",EDGE,"E19.filletArc"),sQuery(id+"F0.wireOp",EDGE,"E20.filletArc"),sQuery(id+"F0.wireOp",EDGE,"E25.0"),sQuery(id+"F0.wireOp",EDGE,"E25.1"),sQuery(id+"F0.wireOp",EDGE,"E25.2"),sQuery(id+"F0.wireOp",EDGE,"E25.3"),sQuery(id+"F0.wireOp",EDGE,"E25.4"),sQuery(id+"F0.wireOp",EDGE,"E25.5"),sQuery(id+"F0.wireOp",EDGE,"E25.6"),sQuery(id+"F0.wireOp",EDGE,"E25.7")])],"isStart":false});
            extrude(context, id + "F17", {"entities" : qUnion([Q0, Q1, Q2, Q3, Q4]), "endBound" : BoundingType.UP_TO_SURFACE, "endBoundEntityFace" : qUnion([Q5]), "depth" : 25 * mm});
        }
    });
